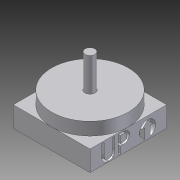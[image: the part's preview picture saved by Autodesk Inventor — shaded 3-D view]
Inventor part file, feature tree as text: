
AUTODESK INVENTOR PART (.ipt)
format: ipt  version: 2011 (Build 150239000, 239)  size: 685,056 bytes
history: native  units: mm
features: sketch x6, extrude x4, emboss x2
ambient origin geometry x8: Origin, YZ Plane, XZ Plane, XY Plane, X Axis, Y Axis, Z Axis, Center Point
feature tree (12):
  extrude  "Extrusion4"  Depth=15.0mm
  extrude  "Extrusion5"  Depth=15.0mm
  emboss  "Emboss1"
  emboss  "Emboss2"
  extrude  "Extrusion7"  Depth=7.5mm
  extrude  "Extrusion8"  Depth=1.0mm TaperAngle=0.0deg
  sketch  "Sketch4"  dims[d14=15.0mm d15=15.0mm]
  sketch  "Sketch5"  dims[d16=4.0mm d17=0.0mm d18=15.0mm]
  sketch  "Sketch7"  dims[d19=7.5mm d20=7.5mm]
  sketch  "Sketch8"  dims[d21=2.5mm d22=0.0mm d38=1.0mm d39=0.0mm]
  sketch  "Sketch9"  dims[d40=1.0mm d41=0.0mm]
  sketch  "Sketch10"  dims[d42=1.9mm d43=13.0mm d44=0.0mm d45=2.0mm d46=15.0mm d47=0.0mm]
